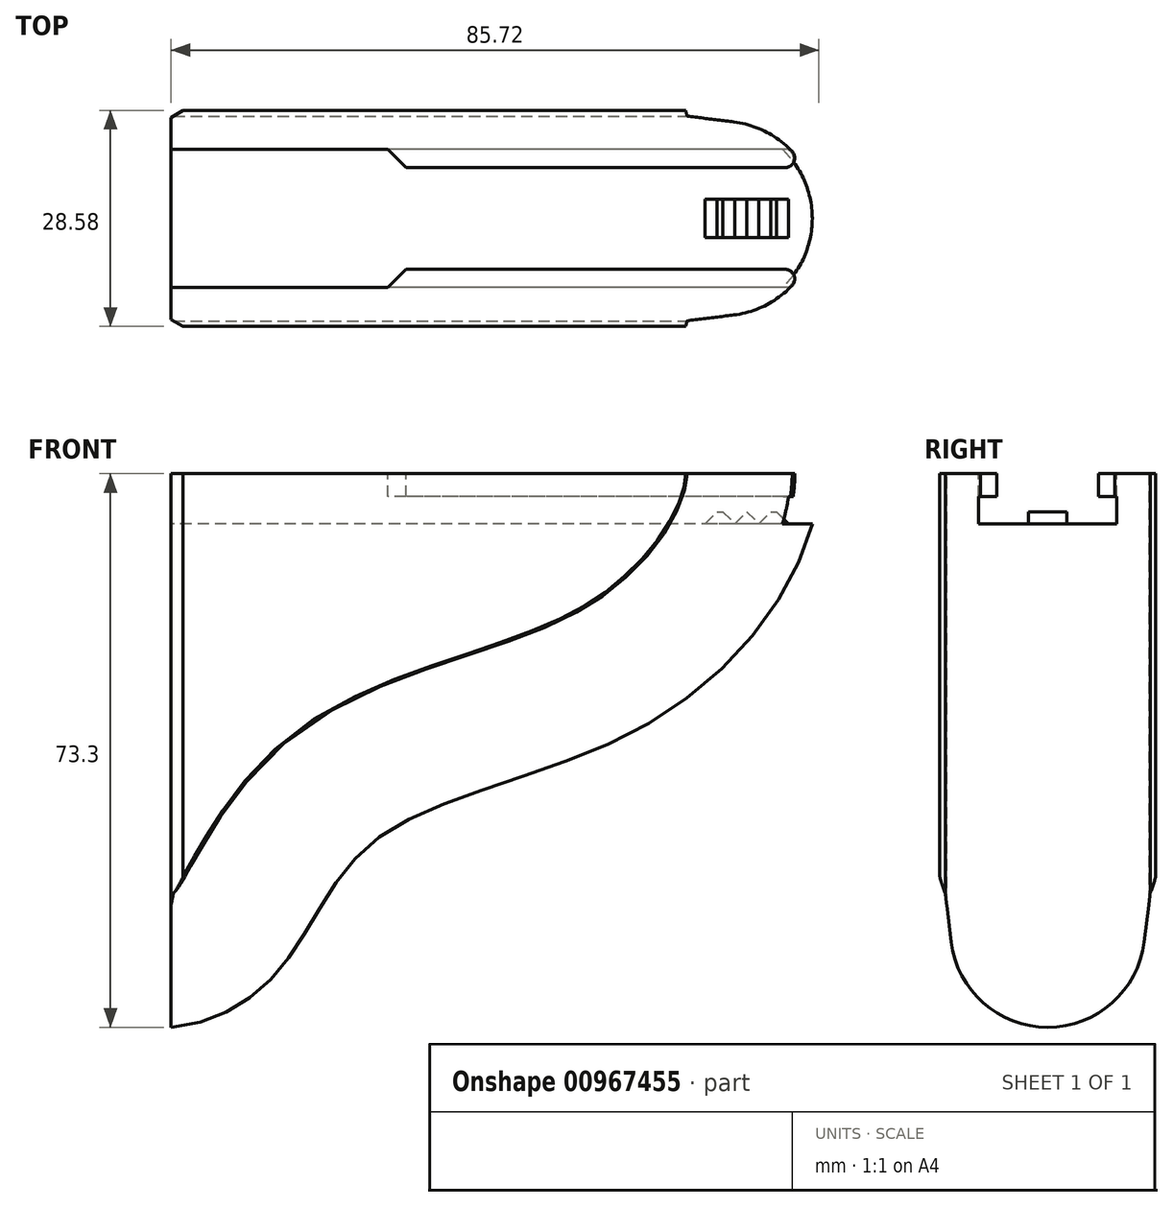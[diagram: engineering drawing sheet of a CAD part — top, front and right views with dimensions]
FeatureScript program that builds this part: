
annotation { "Feature Type Name" : "Feature", "Feature Type Description" : "" }
export const myFeature = defineFeature(function(context is Context, id is Id, definition is map)
    precondition{}
    {
        {
            var Q0;
            Q0=qCreatedBy(makeId("Right.planeOp"),FACE);
            var sketch = newSketch(context, id + "F0", { "sketchPlane" : qUnion([Q0])});
            skLineSegment(sketch, "E0", {"start": v(-9.14, 0) * mm, "end": v(9.14, 0) * mm});
            skLineSegment(sketch, "E1", {"start": v(-9.14, 0) * mm, "end": v(-9.14, 3.57) * mm});
            skLineSegment(sketch, "E2", {"start": v(-9.14, 3.57) * mm, "end": v(-6.73, 3.57) * mm});
            skLineSegment(sketch, "E3", {"start": v(-6.73, 3.57) * mm, "end": v(-6.73, 6.62) * mm});
            skLineSegment(sketch, "E4", {"start": v(-6.73, 6.62) * mm, "end": v(-14.29, 6.62) * mm});
            skLineSegment(sketch, "E5", {"start": v(-14.29, 6.62) * mm, "end": v(-14.29, -66.68) * mm});
            skLineSegment(sketch, "E6", {"start": v(-14.29, -66.68) * mm, "end": v(0, -66.68) * mm});
            skLineSegment(sketch, "E7.MirrorCS", {"start": v(6.73, 3.57) * mm, "end": v(6.73, 6.62) * mm});
            skLineSegment(sketch, "E8.MirrorCS", {"start": v(9.14, 3.57) * mm, "end": v(6.73, 3.57) * mm});
            skLineSegment(sketch, "E9.MirrorCS", {"start": v(9.14, 0) * mm, "end": v(9.14, 3.57) * mm});
            skLineSegment(sketch, "E10.MirrorCS", {"start": v(6.73, 6.62) * mm, "end": v(14.29, 6.62) * mm});
            skLineSegment(sketch, "E11.MirrorCS", {"start": v(14.29, -66.68) * mm, "end": v(0, -66.68) * mm});
            skLineSegment(sketch, "E12.MirrorCS", {"start": v(14.29, 6.62) * mm, "end": v(14.29, -66.68) * mm});
            skSolve(sketch);
        }
        {
            var Q0;
            Q0=qSketchRegion(id+"F0",true);
            extrude(context, id + "F1", {"entities" : qUnion([Q0]), "depth" : 85.72 * mm, "offsetDistance" : 25 * mm});
        }
        {
            var Q0;
            Q0=qCreatedBy(makeId("Right.planeOp"),FACE);
            var sketch = newSketch(context, id + "F2", { "sketchPlane" : qUnion([Q0])});
            skLineSegment(sketch, "E13.bottom", {"start": v(9.14, 0) * mm, "end": v(-9.14, 0) * mm});
            skLineSegment(sketch, "E13.top", {"start": v(9.14, 6.62) * mm, "end": v(-9.14, 6.62) * mm});
            skLineSegment(sketch, "E13.left", {"start": v(9.14, 0) * mm, "end": v(9.14, 6.62) * mm});
            skLineSegment(sketch, "E13.right", {"start": v(-9.14, 0) * mm, "end": v(-9.14, 6.62) * mm});
            skSolve(sketch);
        }
        {
            var Q0;
            Q0 = qSketchRegion(id + "F2", true);
            extrude(context, id + "F3", {"entities" : qUnion([Q0]), "operationType" : NewBodyOperationType.REMOVE, "depth" : 28.57 * mm, "offsetDistance" : 25.4 * mm});
        }
        {
            var Q0;
            Q0=makeQuery(id+"F3.boolean.opBoolean","INTERSECT",EDGE,{"derivedFrom":[makeQuery(id+"F1.opExtrude","SWEPT_FACE",FACE,{"disambiguationData":[OSD([sQuery(id+"F0.wireOp",EDGE,"E7.MirrorCS")])]}),makeQuery(id+"F3.opExtrude","CAP_FACE",FACE,{"disambiguationData":[OSD([sQuery(id+"F2.wireOp",EDGE,"E13.bottom"),sQuery(id+"F2.wireOp",EDGE,"E13.top"),sQuery(id+"F2.wireOp",EDGE,"E13.left"),sQuery(id+"F2.wireOp",EDGE,"E13.right")])],"isStart":false})]});
            var Q1;
            Q1=makeQuery(id+"F3.boolean.opBoolean","INTERSECT",EDGE,{"derivedFrom":[makeQuery(id+"F1.opExtrude","SWEPT_FACE",FACE,{"disambiguationData":[OSD([sQuery(id+"F0.wireOp",EDGE,"E3")])]}),makeQuery(id+"F3.opExtrude","CAP_FACE",FACE,{"disambiguationData":[OSD([sQuery(id+"F2.wireOp",EDGE,"E13.bottom"),sQuery(id+"F2.wireOp",EDGE,"E13.top"),sQuery(id+"F2.wireOp",EDGE,"E13.left"),sQuery(id+"F2.wireOp",EDGE,"E13.right")])],"isStart":false})]});
            chamfer(context, id + "F4", {"entities" : qUnion([Q0, Q1]), "width" : 2.54 * mm, "tangentPropagation" : true});
        }
        {
            var Q0;
            Q0=qCreatedBy(makeId("Front.planeOp"),FACE);
            var sketch = newSketch(context, id + "F5", { "sketchPlane" : qUnion([Q0])});
            skLineSegment(sketch, "E14", {"start": v(70.68, 0) * mm, "end": v(72.26, 1.59) * mm});
            skLineSegment(sketch, "E15", {"start": v(72.26, 1.59) * mm, "end": v(73.02, 1.59) * mm});
            skLineSegment(sketch, "E16", {"start": v(73.02, 1.59) * mm, "end": v(74.61, 0) * mm});
            skLineSegment(sketch, "E17", {"start": v(74.61, 0) * mm, "end": v(76.2, 1.59) * mm});
            skLineSegment(sketch, "E18", {"start": v(76.2, 1.59) * mm, "end": v(77.79, 0) * mm});
            skLineSegment(sketch, "E19", {"start": v(77.79, 0) * mm, "end": v(79.38, 1.59) * mm});
            skLineSegment(sketch, "E20", {"start": v(79.38, 1.59) * mm, "end": v(80.14, 1.59) * mm});
            skLineSegment(sketch, "E21", {"start": v(80.14, 1.59) * mm, "end": v(81.72, 0) * mm});
            skLineSegment(sketch, "E22", {"start": v(81.72, 0) * mm, "end": v(70.68, 0) * mm});
            skSolve(sketch);
        }
        {
            var Q0;
            Q0 = qSketchRegion(id + "F5", true);
            extrude(context, id + "F6", {"entities" : qUnion([Q0]), "operationType" : NewBodyOperationType.ADD, "depth" : 2.54 * mm, "offsetDistance" : 25.4 * mm, "hasSecondDirection" : true, "secondDirectionOppositeDirection" : true, "secondDirectionDepth" : 2.54 * mm});
        }
        {
            var Q0;
            Q0=qCreatedBy(makeId("Front.planeOp"),FACE);
            var sketch = newSketch(context, id + "F7", { "sketchPlane" : qUnion([Q0])});
            skFitSpline(sketch, "E23", {"points": [v(85.73, 6.62) * mm, v(63.82, -26.1) * mm, v(27.24, -41.74) * mm, v(14.94, -58.35) * mm, v(0, -66.68) * mm], "startDerivative": vector(0, -124.33) * mm, "endDerivative": vector(-97.17, -7.9) * mm});
            skLineSegment(sketch, "E24", {"start": v(85.73, 6.62) * mm, "end": v(85.73, -66.67) * mm});
            skLineSegment(sketch, "E25", {"start": v(85.73, -66.67) * mm, "end": v(0, -66.67) * mm});
            skSolve(sketch);
        }
        {
            var Q0;
            Q0=qCreatedBy(makeId("Right.planeOp"),FACE);
            var sketch = newSketch(context, id + "F8", { "sketchPlane" : qUnion([Q0])});
            skLineSegment(sketch, "E26", {"start": v(14.29, -48.87) * mm, "end": v(13.55, -49.07) * mm});
            skLineSegment(sketch, "E27", {"start": v(13.55, -49.07) * mm, "end": v(12.78, -55.37) * mm});
            skArc(sketch, "E28", {"start": v(0, -66.68) * mm, "mid": v(8.53, -63.44) * mm, "end": v(12.78, -55.37) * mm});
            skLineSegment(sketch, "E29", {"start": v(14.29, -48.87) * mm, "end": v(14.29, -66.68) * mm});
            skLineSegment(sketch, "E30", {"start": v(14.29, -66.68) * mm, "end": v(0, -66.68) * mm});
            skLineSegment(sketch, "E31.MirrorCS", {"start": v(-14.29, -48.87) * mm, "end": v(-13.55, -49.07) * mm});
            skArc(sketch, "E32.MirrorCS", {"start": v(0, -66.68) * mm, "mid": v(-8.53, -63.44) * mm, "end": v(-12.78, -55.37) * mm});
            skLineSegment(sketch, "E33.MirrorCS", {"start": v(-14.29, -48.87) * mm, "end": v(-14.29, -66.68) * mm});
            skLineSegment(sketch, "E34.MirrorCS", {"start": v(-13.55, -49.07) * mm, "end": v(-12.78, -55.37) * mm});
            skLineSegment(sketch, "E35.MirrorCS", {"start": v(-14.29, -66.68) * mm, "end": v(0, -66.68) * mm});
            skSolve(sketch);
        }
        {
            var Q0;
            Q0 = qSketchRegion(id + "F7", true);
            extrude(context, id + "F9", {"entities" : qUnion([Q0]), "operationType" : NewBodyOperationType.REMOVE, "endBound" : BoundingType.UP_TO_NEXT, "oppositeDirection" : true, "depth" : 25.4 * mm, "offsetDistance" : 25.4 * mm, "hasSecondDirection" : true, "secondDirectionBound" : SecondDirectionBoundingType.UP_TO_NEXT, "secondDirectionOppositeDirection" : false, "secondDirectionDepth" : 25.4 * mm});
        }
        {
            var Q0;
            Q0 = qSketchRegion(id + "F8", true);
            var Q1;
            Q1=sQuery(id+"F7.wireOp",EDGE,"E23");
            sweep(context, id + "F10", {"operationType" : NewBodyOperationType.REMOVE, "profiles" : qUnion([Q0]), "path" : qUnion([Q1])});
        }
        {
            var Q0;
            Q0=makeQuery(id+"F1.opExtrude","CAP_EDGE",EDGE,{"disambiguationData":[OSD([sQuery(id+"F0.wireOp",EDGE,"E5")])],"isStart":true});
            var Q1;
            Q1=makeQuery(id+"F10.boolean.opBoolean","COPY",EDGE,{"derivedFrom":makeQuery(id+"F10.opSweep","CAP_EDGE",EDGE,{"disambiguationData":[OSD([sQuery(id+"F7.wireOp",VERTEX,"E23.end"),sQuery(id+"F8.wireOp",EDGE,"E31.MirrorCS")])],"isStart":true})});
            var Q2;
            Q2=makeQuery(id+"F10.boolean.opBoolean","COPY",EDGE,{"derivedFrom":makeQuery(id+"F10.opSweep","CAP_EDGE",EDGE,{"disambiguationData":[OSD([sQuery(id+"F7.wireOp",VERTEX,"E23.end"),sQuery(id+"F8.wireOp",EDGE,"E34.MirrorCS")])],"isStart":true})});
            var Q3;
            Q3=makeQuery(id+"F10.boolean.opBoolean","COPY",EDGE,{"derivedFrom":makeQuery(id+"F10.opSweep","CAP_EDGE",EDGE,{"disambiguationData":[OSD([sQuery(id+"F7.wireOp",VERTEX,"E23.end"),sQuery(id+"F8.wireOp",EDGE,"E32.MirrorCS")])],"isStart":true})});
            var Q4;
            Q4=makeQuery(id+"F10.boolean.opBoolean","COPY",EDGE,{"derivedFrom":makeQuery(id+"F10.opSweep","CAP_EDGE",EDGE,{"disambiguationData":[OSD([sQuery(id+"F7.wireOp",VERTEX,"E23.end"),sQuery(id+"F8.wireOp",EDGE,"E28")])],"isStart":true})});
            var Q5;
            Q5=makeQuery(id+"F10.boolean.opBoolean","COPY",EDGE,{"derivedFrom":makeQuery(id+"F10.opSweep","CAP_EDGE",EDGE,{"disambiguationData":[OSD([sQuery(id+"F7.wireOp",VERTEX,"E23.end"),sQuery(id+"F8.wireOp",EDGE,"E27")])],"isStart":true})});
            var Q6;
            Q6=makeQuery(id+"F10.boolean.opBoolean","COPY",EDGE,{"derivedFrom":makeQuery(id+"F10.opSweep","CAP_EDGE",EDGE,{"disambiguationData":[OSD([sQuery(id+"F7.wireOp",VERTEX,"E23.end"),sQuery(id+"F8.wireOp",EDGE,"E26")])],"isStart":true})});
            var Q7;
            Q7=makeQuery(id+"F1.opExtrude","CAP_EDGE",EDGE,{"disambiguationData":[OSD([sQuery(id+"F0.wireOp",EDGE,"E12.MirrorCS")])],"isStart":true});
            chamfer(context, id + "F11", {"entities" : qUnion([Q0, Q1, Q2, Q3, Q4, Q5, Q6, Q7]), "chamferType" : ChamferType.OFFSET_ANGLE, "width" : 1.59 * mm, "oppositeDirection" : false, "angle" : 30 * degree, "tangentPropagation" : true});
        }
        {
            var Q0;
            Q0=makeQuery(id+"F10.boolean.opBoolean","INTERSECT",EDGE,{"derivedFrom":[makeQuery(id+"F1.opExtrude","SWEPT_FACE",FACE,{"disambiguationData":[OSD([sQuery(id+"F0.wireOp",EDGE,"E7.MirrorCS")])]}),makeQuery(id+"F10.opSweep","SWEPT_FACE",FACE,{"disambiguationData":[OSD([sQuery(id+"F7.wireOp",EDGE,"E23"),sQuery(id+"F8.wireOp",EDGE,"E28")])]})]});
            var Q1;
            Q1=makeQuery(id+"F10.boolean.opBoolean","INTERSECT",EDGE,{"derivedFrom":[makeQuery(id+"F1.opExtrude","SWEPT_FACE",FACE,{"disambiguationData":[OSD([sQuery(id+"F0.wireOp",EDGE,"E3")])]}),makeQuery(id+"F10.opSweep","SWEPT_FACE",FACE,{"disambiguationData":[OSD([sQuery(id+"F7.wireOp",EDGE,"E23"),sQuery(id+"F8.wireOp",EDGE,"E32.MirrorCS")])]})]});
            fillet(context, id + "F12", {"entities" : qUnion([Q0, Q1]), "radius" : 1.27 * mm, "allowEdgeOverflow" : false});
        }
    });
